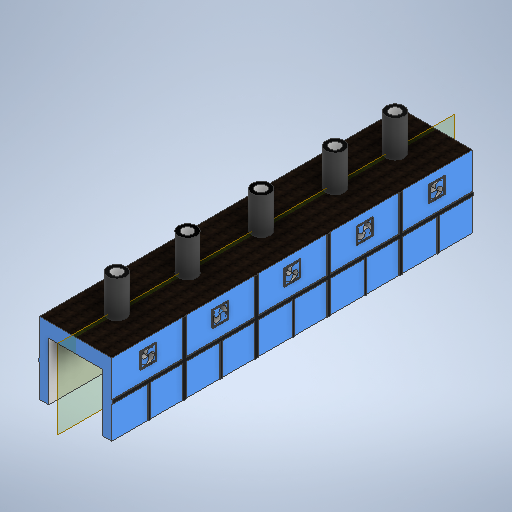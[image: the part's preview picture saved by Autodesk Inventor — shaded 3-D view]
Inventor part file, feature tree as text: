
AUTODESK INVENTOR PART (.ipt)
format: ipt  version: 2025.2 (Build 292293000, 293)  size: 811,008 bytes
history: native  units: mm
features: sketch x5, extrude x4, plane x2, projected_geometry x2, mirror x1
ambient origin geometry x8: Origin, YZ Plane, XZ Plane, XY Plane, X Axis, Y Axis, Z Axis, Center Point
bodies: Solid1 (feature_tree)
feature tree (14):
  extrude  "Extrusion1"  Depth=10000.0mm
  extrude  "Extrusion2"  Depth=2000.0mm
  sketch  "Sketch3"  dims[d4=2000.0mm d5=2000.0mm]
  plane  "Work Plane1"
  mirror  "Mirror1"
  extrude  "Extrusion3"  Depth=2000.0mm
  extrude  "Extrusion4"  Depth=400.0mm
  sketch  "Sketch1"  dims[d0=2000.0mm d1=10000.0mm]
  sketch  "Sketch2"  dims[d2=100.0mm d3=2000.0mm]
  projected_geometry  "Projected Loop1"
  plane  "Work Plane2"
  sketch  "Sketch5"  dims[d6=2000.0mm d7=400.0mm]
  projected_geometry  "Projected Loop2"
  sketch  "Sketch6"  dims[d9=100.0mm d10=100.0mm d11=100.0mm d12=100.0mm d13=100.0mm d14=100.0mm d15=100.0mm d16=100.0mm d17=100.0mm d18=100.0mm d19=100.0mm d20=100.0mm d21=100.0mm d22=100.0mm d23=100.0mm d24=100.0mm d25=2000.0mm d26=0.0mm d31=2000.0mm d32=2000.0mm d33=2000.0mm d34=2000.0mm d35=100.0mm d36=100.0mm d37=100.0mm d38=100.0mm d39=50.0mm d40=50.0mm d41=50.0mm d42=50.0mm d43=50.0mm d44=20.0mm d45=0.0mm d46=250.0mm d47=250.0mm d48=0.0mm d49=0.0mm d50=500.0mm d51=500.0mm d52=500.0mm d53=500.0mm d54=500.0mm d55=300.0mm d56=300.0mm d57=300.0mm d58=300.0mm d59=300.0mm d60=1000.0mm d61=0.0mm]
